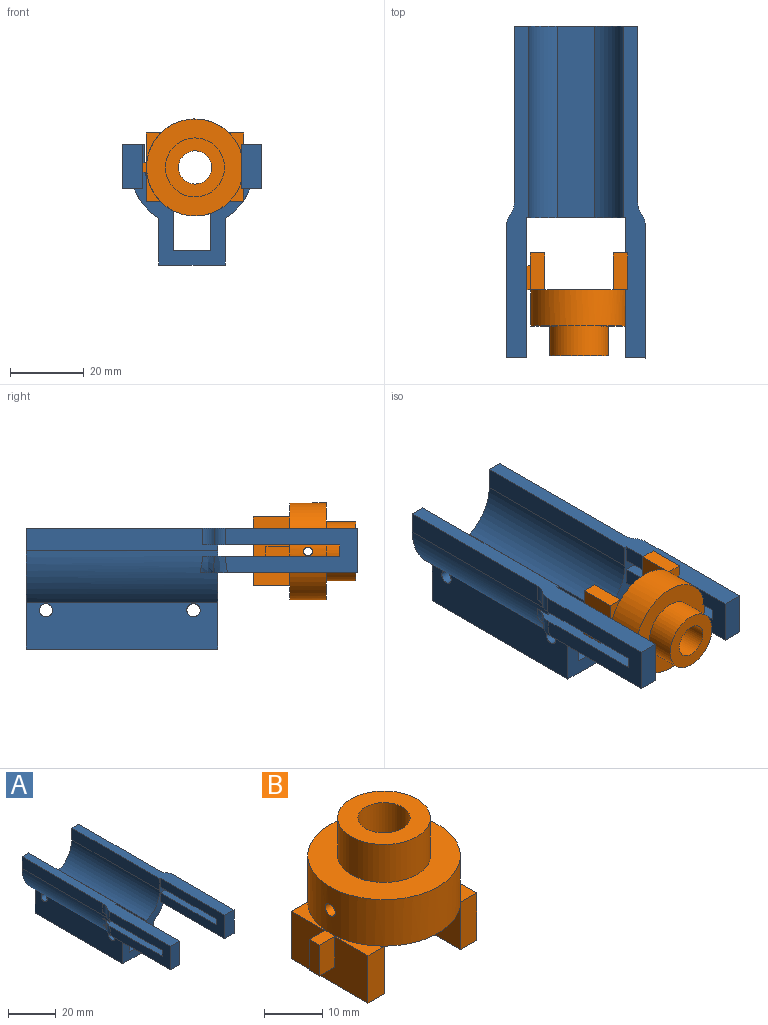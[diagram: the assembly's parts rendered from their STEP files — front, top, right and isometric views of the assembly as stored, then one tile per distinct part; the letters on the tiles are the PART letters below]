
ASSEMBLY  parts=2 mates=1
PART A: 44 faces, bbox 37.8x90.2x32.9 mm
  f0: plane 33.5x32.71mm, normal (0,-1,0), area 267.3mm2, adj f1,f2,f3,f4,f5,f6,f7,f8
  f1: cylinder r=16.75mm len=52mm, axis (0,-1,0), area 850.5mm2, adj f0,f2,f16,f17,f22,f31,f36
  f2: plane 52x12.61mm, normal (-1,0,0), area 635.5mm2, adj f0,f1,f3,f17,f18,f19
  f3: plane 52x18.1mm, normal (0,0,-1), area 941.2mm2, adj f0,f2,f4,f17
  f4: plane 52x12.61mm, normal (1,0,0), area 635.5mm2, adj f0,f3,f5,f17,f20,f21
  f5: cylinder r=16.75mm len=52mm, axis (0,-1,0), area 850.5mm2, adj f0,f4,f6,f17,f26,f30,f37
  f6: plane 52x6mm, normal (1,0,0), area 293.8mm2, adj f0,f5,f7,f17,f29,f39
  f7: plane 90x6.05mm, normal (0,0,1), area 419.1mm2, adj f0,f6,f8,f17,f25,f27,f34,f39
  f8: plane 52x6mm, normal (-1,0,0), area 312mm2, adj f0,f7,f9,f17
  f9: cylinder r=12.75mm len=52mm, axis (0,-1,0), area 771.4mm2, adj f0,f8,f10,f17
  f10: plane 52x11mm, normal (-1,0,0), area 551.6mm2, adj f0,f9,f11,f17,f20,f21
  f11: plane 52x10.1mm, normal (0,0,1), area 525.2mm2, adj f0,f10,f12,f17
  f12: plane 52x11mm, normal (1,0,0), area 551.6mm2, adj f0,f11,f13,f17,f18,f19
  f13: cylinder r=12.75mm len=52mm, axis (0,-1,0), area 771.4mm2, adj f0,f12,f14,f17
  f14: plane 52x6mm, normal (1,0,0), area 312mm2, adj f0,f13,f15,f17
  f15: plane 90x6.05mm, normal (0,0,1), area 419.1mm2, adj f0,f14,f16,f17,f23,f24,f35,f38
  f16: plane 52x6mm, normal (-1,0,0), area 293.8mm2, adj f0,f1,f15,f17,f32,f38
  f17: plane 33.5x32.71mm, normal (0,1,0), area 325mm2, adj f1,f2,f3,f4,f5,f6,f7,f8
  f18: cylinder r=1.8mm len=4mm, axis (1,0,0), area 45.2mm2, adj f2,f12
  f19: cylinder r=1.8mm len=4mm, axis (1,0,0), area 45.2mm2, adj f2,f12
  f20: cylinder r=1.8mm len=4mm, axis (1,0,0), area 45.2mm2, adj f4,f10
  f21: cylinder r=1.8mm len=4mm, axis (1,0,0), area 45.2mm2, adj f4,f10
  f22: plane 42.96x5.69mm, normal (0,0,-1), area 212.5mm2, adj f0,f1,f23,f24,f35,f36,f41
  f23: plane 38x12mm, normal (1,0,0), area 357mm2, adj f0,f15,f22,f24,f31,f32,f33
  f24: plane 12x5.5mm, normal (0,-1,0), area 66mm2, adj f15,f22,f23,f35
  f25: plane 38x12mm, normal (-1,0,0), area 357mm2, adj f0,f7,f26,f27,f28,f29,f30
  f26: plane 42.96x5.69mm, normal (0,0,-1), area 212.5mm2, adj f0,f5,f25,f27,f34,f37,f43
  f27: plane 12x5.5mm, normal (0,-1,0), area 66mm2, adj f7,f25,f26,f34
  f28: plane 5.5x3mm, normal (0,1,0), area 16.5mm2, adj f25,f29,f30,f34
  f29: plane 37.04x5.5mm, normal (0,0,-1), area 183.6mm2, adj f0,f6,f25,f28,f34,f39,f42
  f30: plane 37.14x5.54mm, normal (0,0,1), area 183.7mm2, adj f0,f5,f25,f28,f34,f37,f43
  f31: plane 37.14x5.54mm, normal (0,0,1), area 183.7mm2, adj f0,f1,f23,f33,f35,f36,f41
  f32: plane 37.04x5.5mm, normal (0,0,-1), area 183.6mm2, adj f0,f16,f23,f33,f35,f38,f40
  f33: plane 5.5x3mm, normal (0,1,0), area 16.5mm2, adj f23,f31,f32,f35
  f34: plane 35.97x12mm, normal (1,0,0), area 337.6mm2, adj f7,f26,f27,f28,f29,f30,f42,f43
  f35: plane 35.97x12mm, normal (-1,0,0), area 337.6mm2, adj f15,f22,f24,f31,f32,f33,f40,f41
  f36: bspline ~8.63x4.85mm, area 16.5mm2, adj f1,f22,f31,f41
  f37: bspline ~8.66x4.91mm, area 16.5mm2, adj f5,f26,f30,f43
  f38: cylinder r=5mm len=4.5mm, axis (0,0,1), area 14.7mm2, adj f15,f16,f32,f40
  f39: cylinder r=5mm len=4.5mm, axis (0,0,1), area 14.7mm2, adj f6,f7,f29,f42
  f40: cylinder r=5mm len=4.5mm, axis (0,0,1), area 14.7mm2, adj f15,f32,f35,f38
  f41: bspline ~6.3x3.77mm, area 16.5mm2, adj f22,f31,f35,f36
  f42: cylinder r=5mm len=4.5mm, axis (0,0,1), area 14.7mm2, adj f7,f29,f34,f39
  f43: bspline ~6.91x3.77mm, area 16.5mm2, adj f26,f30,f34,f37
PART B: 47 faces, bbox 34.2x26.3x27.8 mm
  f0: plane 2.65x1.23mm, normal (0,1,0), area 3.3mm2, adj f2,f14,f19,f46
  f1: plane 2.65x1.23mm, normal (0,-1,0), area 3.3mm2, adj f2,f14,f19,f46
  f2: plane 1.65x1.23mm, normal (1,0,0), area 1.7mm2, adj f0,f1,f19,f46
  f3: plane 4.03x2.65mm, normal (0,-1,0), area 10.7mm2, adj f7,f14,f26,f45
  f4: plane 4.03x2.65mm, normal (0,1,0), area 10.7mm2, adj f8,f14,f26,f45
  f5: plane 1.65x1.23mm, normal (-1,0,0), area 1.7mm2, adj f24,f25,f27,f45
  f6: plane 18.69x10mm, normal (-1,0,0), area 170.7mm2, adj f33,f34,f35,f36,f37,f38,f39
  f7: plane 18.5x12.33mm, normal (0,0,-1), area 147.6mm2, adj f3,f14,f15,f17,f18,f26
  f8: plane 18.5x12.33mm, normal (0,0,-1), area 144.9mm2, adj f4,f14,f15,f16,f18,f20,f21,f22
  f9: plane 13.3x13.3mm, normal (0,0,-1), area 75.3mm2, adj f10,f14
  f10: cylinder r=4.5mm len=9mm, axis (0,0,-1), area 226.2mm2, adj f9,f12
  f11: cylinder r=8mm len=16mm, axis (0,0,-1), area 402.1mm2, adj f12,f13
  f12: plane 16x16mm, normal (0,0,1), area 137.4mm2, adj f10,f11
  f13: plane 26.3x26.3mm, normal (0,0,1), area 342.2mm2, adj f11,f15
  f14: cylinder r=6.65mm len=13.3mm, axis (0,0,1), area 372.9mm2, adj f0,f1,f3,f4,f7,f8,f9,f16
  f15: cylinder r=13.15mm len=26.3mm, axis (0,0,1), area 800.7mm2, adj f7,f8,f13,f32,f36,f45,f46
  f16: plane 4.03x2.65mm, normal (0,1,0), area 10.7mm2, adj f8,f14,f18,f46
  f17: plane 4.03x2.65mm, normal (0,-1,0), area 10.7mm2, adj f7,f14,f18,f46
  f18: plane 18.69x14.03mm, normal (1,0,0), area 193.2mm2, adj f7,f8,f16,f17,f33,f34,f35,f46
  f19: plane 2.65x1.65mm, normal (0,0,-1), area 4.3mm2, adj f0,f1,f2,f14
  f20: plane 7x1.65mm, normal (-1,0,0), area 11.6mm2, adj f8,f14,f22,f23
  f21: plane 7x1.65mm, normal (1,0,0), area 11.6mm2, adj f8,f14,f22,f23
  f22: plane 7x1.65mm, normal (0,1,0), area 11.5mm2, adj f8,f20,f21,f23
  f23: plane 1.65x1.65mm, normal (0,0,-1), area 2.7mm2, adj f14,f20,f21,f22
  f24: plane 2.65x1.23mm, normal (0,-1,0), area 3.3mm2, adj f5,f14,f27,f45
  f25: plane 2.65x1.23mm, normal (0,1,0), area 3.3mm2, adj f5,f14,f27,f45
  f26: plane 18.69x14.03mm, normal (-1,0,0), area 193.2mm2, adj f3,f4,f7,f8,f28,f30,f31,f45
  f27: plane 2.65x1.65mm, normal (0,0,-1), area 4.3mm2, adj f5,f14,f24,f25
  f28: plane 10x4mm, normal (0,1,0), area 40mm2, adj f26,f29,f31,f32
  f29: plane 18.69x10mm, normal (1,0,0), area 170.7mm2, adj f28,f30,f31,f32,f41,f42,f43
  f30: plane 10x4mm, normal (0,-1,0), area 40mm2, adj f26,f29,f31,f32
  f31: plane 18.69x4mm, normal (0,0,-1), area 74.8mm2, adj f26,f28,f29,f30
  f32: plane 18.69x8mm, normal (0,0,1), area 34.5mm2, adj f15,f28,f29,f30,f41,f42,f44
  f33: plane 10x4mm, normal (0,-1,0), area 40mm2, adj f6,f18,f35,f36
  f34: plane 10x4mm, normal (0,1,0), area 40mm2, adj f6,f18,f35,f36
  f35: plane 18.69x4mm, normal (0,0,-1), area 74.8mm2, adj f6,f18,f33,f34
  f36: plane 18.69x7.7mm, normal (0,0,1), area 33.8mm2, adj f6,f15,f33,f34,f37,f38,f40
  f37: plane 6.5x3.7mm, normal (0,1,0), area 24mm2, adj f6,f36,f39,f40
  f38: plane 6.5x3.7mm, normal (0,-1,0), area 24mm2, adj f6,f36,f39,f40
  f39: plane 3.7x2.5mm, normal (0,0,-1), area 9.3mm2, adj f6,f37,f38,f40
  f40: plane 6.5x2.5mm, normal (-1,0,0), area 16.2mm2, adj f36,f37,f38,f39
  f41: plane 6.5x4mm, normal (0,1,0), area 26mm2, adj f29,f32,f43,f44
  f42: plane 6.5x4mm, normal (0,-1,0), area 26mm2, adj f29,f32,f43,f44
  f43: plane 4x2.5mm, normal (0,0,-1), area 10mm2, adj f29,f41,f42,f44
  f44: plane 6.5x2.5mm, normal (1,0,0), area 16.2mm2, adj f32,f41,f42,f43
  f45: cylinder r=1.2mm len=6.61mm, axis (1,0,0), area 39.7mm2, adj f3,f4,f5,f14,f15,f24,f25,f26
  f46: cylinder r=1.2mm len=6.61mm, axis (1,0,0), area 39.7mm2, adj f0,f1,f2,f14,f15,f16,f17,f18
PLACE A rot(axis=(0.28,0.96,-0.09),0deg) t=(-0.62,-20.76,-2.55)mm
PLACE B rot(axis=(1,0,0),90deg) t=(0.2,-50.1,8.91)mm
MATE fastened B.f42 <-> A.f30  axis (0,0,-1) through (15.45,-37.05,7.66)mm
